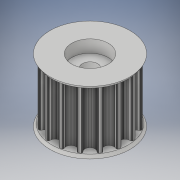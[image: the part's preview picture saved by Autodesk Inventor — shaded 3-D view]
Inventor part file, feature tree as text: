
AUTODESK INVENTOR PART (.ipt)
format: ipt  version: 2019 (Build 230136000, 136)  size: 1,440,768 bytes
history: native  units: mm
features: sketch x8, extrude x4, plane x2, loft x2
ambient origin geometry x8: Origin, YZ Plane, XZ Plane, XY Plane, X Axis, Y Axis, Z Axis, Center Point
bodies: Solid1 (feature_tree)
feature tree (16):
  extrude  "Extrusion1"  Depth=30.0mm
  sketch  "Sketch2"  dims[d3=1.5mm d4=42.0mm]
  plane  "Work Plane1"
  loft  "Loft1"
  sketch  "Sketch4"  dims[d9=40.0mm d10=1.5mm]
  plane  "Work Plane2"
  loft  "Loft2"
  extrude  "Extrusion8"  Depth=1.5mm
  extrude  "Extrusion9"  TaperAngle=0.0deg  [1 undecoded]
  extrude  "Extrusion10"  Depth=19.1mm
  sketch  "Sketch1"  dims[d0=30.0mm d1=0.0mm d2=40.0mm]
  sketch  "Sketch3"  dims[d5=0.0mm d6=90.0deg d7=0.0mm d8=90.0deg]
  sketch  "Sketch5"  dims[d11=42.0mm d12=0.0mm d13=90.0deg]
  sketch  "Sketch13"  dims[d14=0.0mm d15=90.0deg d57=19.1mm]
  sketch  "Sketch17"  dims[d58=6.5mm d59=0.0mm]
  sketch  "Sketch18"  dims[d60=19.1mm d61=6.5mm d62=0.0mm d63=8.0mm d64=6.5mm d65=0.0mm]
note: 1 required parameter value undecoded (feature->parameter linkage not recoverable at this tier; creation-order binding heuristic only, values carry confidence <= 0.55)
